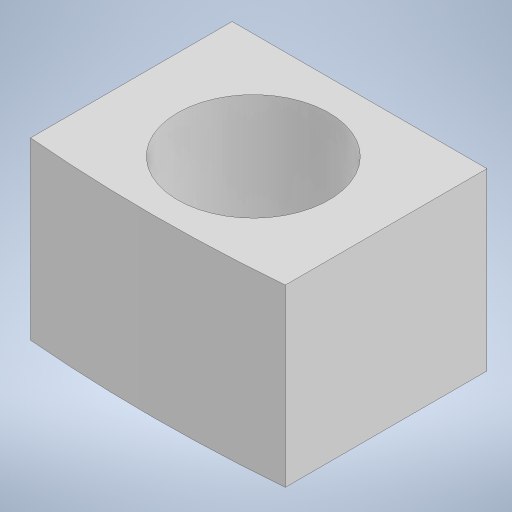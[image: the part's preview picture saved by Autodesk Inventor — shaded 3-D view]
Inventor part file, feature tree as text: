
AUTODESK INVENTOR PART (.ipt)
format: ipt  version: 2024 (Build 280153000, 153)  size: 173,056 bytes
history: native  units: mm
features: extrude x1, sketch x1
ambient origin geometry x8: Origin, YZ Plane, XZ Plane, XY Plane, X Axis, Y Axis, Z Axis, Center Point
bodies: Solid1 (feature_tree)
feature tree (2):
  extrude  "Extrusion1"  Depth=5.5mm
  sketch  "Sketch1"  dims[d0=100.0mm d1=93.0mm d2=4.75mm d6=40.0mm d8=4.0mm d10=4.0mm d11=4.0mm d12=0.0mm d13=5.5mm d14=0.0mm]
